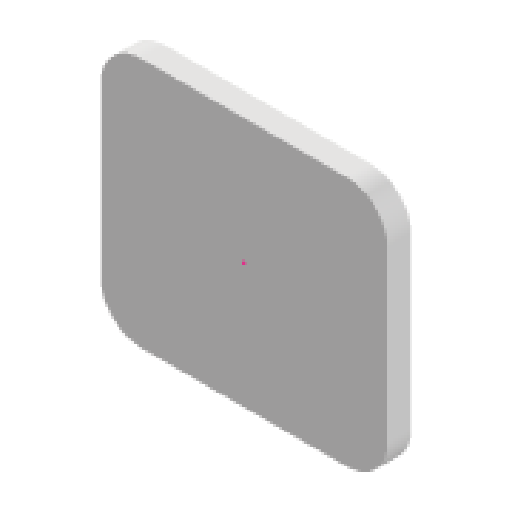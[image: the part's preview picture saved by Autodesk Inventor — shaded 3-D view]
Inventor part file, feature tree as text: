
AUTODESK INVENTOR PART (.ipt)
format: ipt  version: 2025 (Build 290162000, 162)  size: 269,824 bytes
history: native  units: mm
features: reference x33, sketch x9, extrude x6, other x6, fillet x2, sweep x1, projected_geometry x1
ambient origin geometry x8: Origin, YZ Plane, XZ Plane, XY Plane, X Axis, Y Axis, Z Axis, Center Point
bodies: Solid1 (feature_tree)
feature tree (58):
  extrude  "Extrusion1"  Depth=50.0mm
  extrude  "Extrusion2"  Depth=4.0mm
  extrude  "Extrusion3"  Depth=0.1mm
  extrude  "Extrusion4"  Depth=2.1mm TaperAngle=0.0deg
  sketch  "Sketch7"  dims[d14=0.15mm d15=4.0mm d16=1.6mm]
  sketch  "Sketch8"  dims[d17=0.6mm d18=0.22mm]
  sweep  "Sweep1"
  fillet  "Fillet1"  Radius=1.6mm
  extrude  "Extrusion5"  Depth=0.22mm
  extrude  "Extrusion6"  Depth=0.02mm
  fillet  "Fillet2"  Radius=0.4mm
  sketch  "Sketch1"  dims[d0=60.0mm d1=50.0mm]
  sketch  "Sketch2"  dims[d2=4.0mm d3=0.0mm d4=2.8mm]
  reference  "Reference1"
  reference  "Reference2"
  reference  "Reference3"
  reference  "Reference4"
  reference  "Reference5"
  reference  "Reference6"
  reference  "Reference7"
  reference  "Reference8"
  sketch  "Sketch5"  dims[d5=10.0mm d6=0.0mm d7=0.1mm]
  reference  "Reference18"
  reference  "Reference19"
  reference  "Reference20"
  reference  "Reference21"
  reference  "Reference22"
  reference  "Reference23"
  reference  "Reference24"
  reference  "Reference25"
  sketch  "Sketch6"  dims[d8=3.3mm d9=0.0mm d12=2.1mm d13=0.0mm]
  reference  "Reference26"
  reference  "Reference27"
  reference  "Reference28"
  reference  "Reference29"
  reference  "Reference30"
  reference  "Reference31"
  reference  "Reference32"
  reference  "Reference33"
  reference  "Reference34"
  projected_geometry  "Projected Loop1"
  sketch  "3D Sketch1"
  sketch  "Sketch9"  dims[d19=0.0mm d20=0.0mm d21=0.02mm d22=0.4mm]
  reference  "Reference35"
  reference  "Reference36"
  reference  "Reference37"
  reference  "Reference38"
  reference  "Reference39"
  reference  "Reference40"
  reference  "Reference41"
  reference  "Reference42"
  sketch  "Sketch12"  dims[d23=0.4mm d24=0.0mm d25=0.0mm d35=2.0mm d36=7.0mm d37=0.0mm d38=2.0mm]
  other  "USB_C_PD_PPS_sink_with_enclosure.iam"
  other  "top_enclosure:1"
  other  "Plexi-glass:1"
  other  "USB_C_PD_PPS_sink:1"
  other  "3461AS_3461AS-1:2"
  other  "3461AS_3461AS-1:1"
